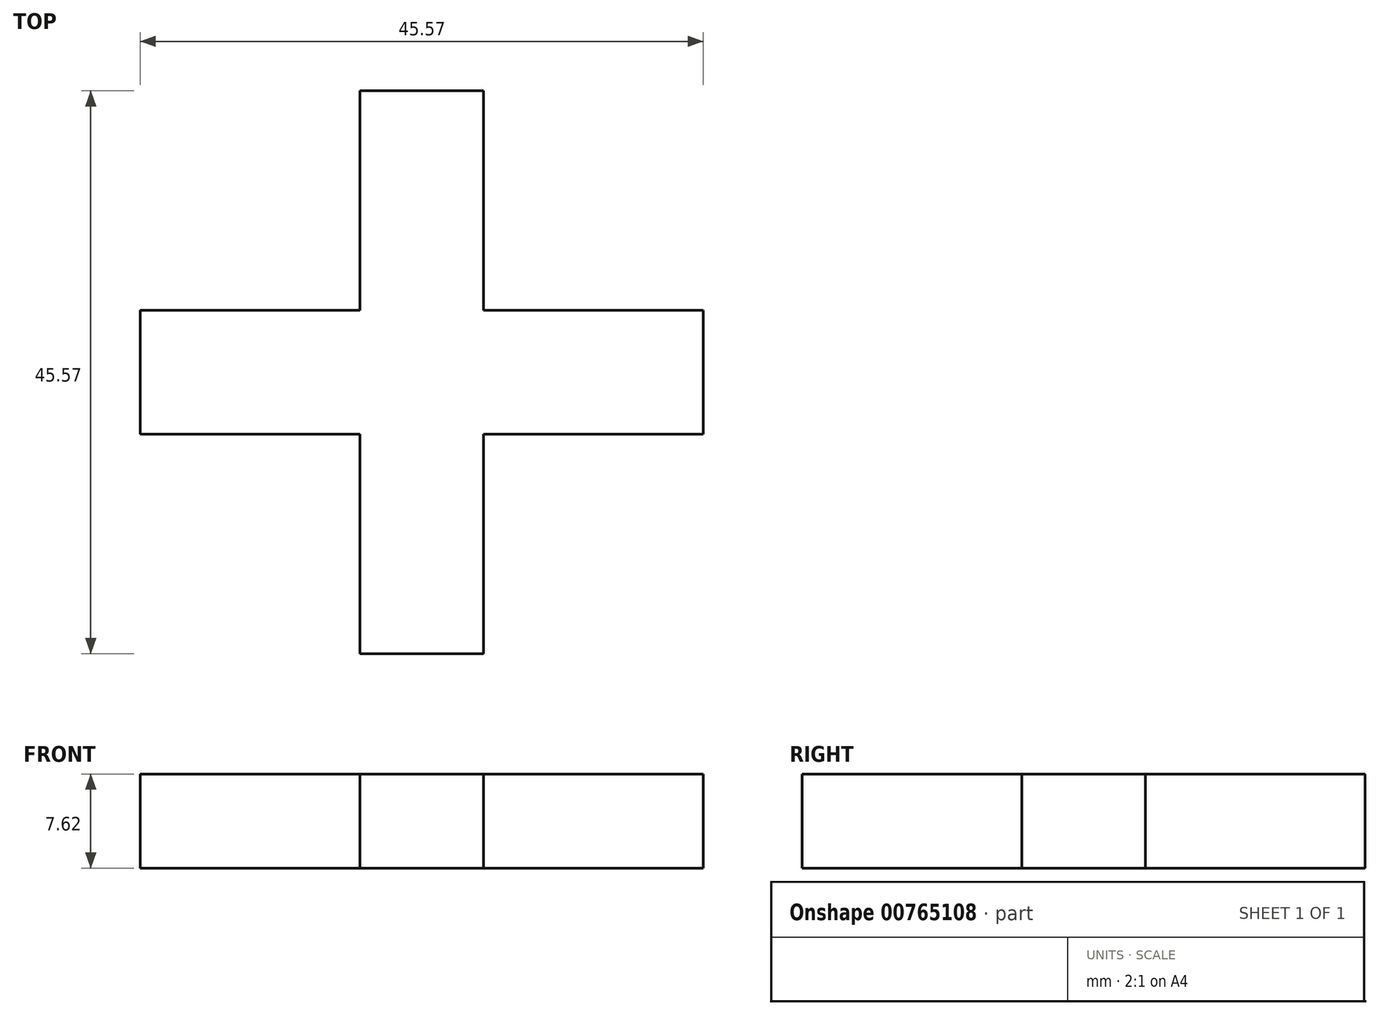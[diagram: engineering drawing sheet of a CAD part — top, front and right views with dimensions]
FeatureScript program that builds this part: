
annotation { "Feature Type Name" : "Feature", "Feature Type Description" : "" }
export const myFeature = defineFeature(function(context is Context, id is Id, definition is map)
    precondition{}
    {
        {
            var Q0;
            Q0=qCreatedBy(makeId("Top.planeOp"),FACE);
            var sketch = newSketch(context, id + "F0", { "sketchPlane" : qUnion([Q0])});
            skLineSegment(sketch, "E0", {"start": v(-2.37, 27.79) * mm, "end": v(7.64, 27.79) * mm});
            skLineSegment(sketch, "E1", {"start": v(7.64, 27.79) * mm, "end": v(7.64, 10) * mm});
            skLineSegment(sketch, "E2", {"start": v(7.64, 10) * mm, "end": v(25.42, 10) * mm});
            skLineSegment(sketch, "E3", {"start": v(25.42, 10) * mm, "end": v(25.42, 0) * mm});
            skLineSegment(sketch, "E4", {"start": v(25.42, 0) * mm, "end": v(7.64, 0) * mm});
            skLineSegment(sketch, "E5", {"start": v(7.64, 0) * mm, "end": v(7.64, -17.78) * mm});
            skLineSegment(sketch, "E6", {"start": v(7.64, -17.78) * mm, "end": v(-2.37, -17.78) * mm});
            skLineSegment(sketch, "E7", {"start": v(-2.37, -17.78) * mm, "end": v(-2.37, 0) * mm});
            skLineSegment(sketch, "E8", {"start": v(-2.37, 0) * mm, "end": v(-20.15, 0) * mm});
            skLineSegment(sketch, "E9", {"start": v(-20.15, 0) * mm, "end": v(-20.15, 10) * mm});
            skLineSegment(sketch, "E10", {"start": v(-20.15, 10) * mm, "end": v(-2.37, 10) * mm});
            skLineSegment(sketch, "E11", {"start": v(-2.37, 10) * mm, "end": v(-2.37, 27.79) * mm});
            skSolve(sketch);
        }
        {
            var Q0;
            Q0=makeQuery(id+"F0.imprint","IMPRINT",FACE,{"disambiguationData":[TD([[makeQuery(id+"F0.imprint","IMPRINT",EDGE,{"derivedFrom":sQuery(id+"F0.wireOp",EDGE,"E0")}),-1.0]])]});
            extrude(context, id + "F1", {"entities" : qUnion([Q0]), "depth" : 7.62 * mm, "offsetDistance" : 25.4 * mm});
        }
    });
